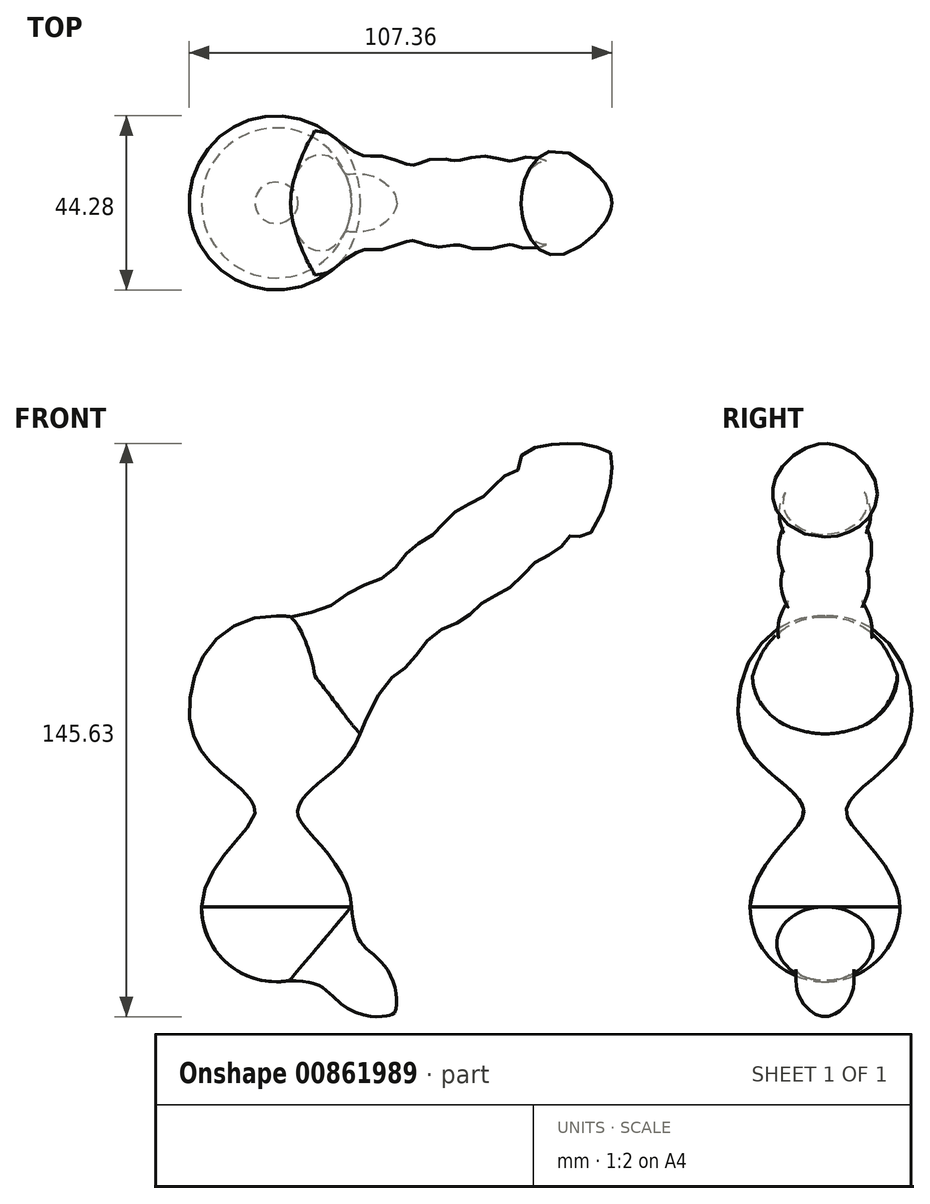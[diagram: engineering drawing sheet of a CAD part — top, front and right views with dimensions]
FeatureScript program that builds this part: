
annotation { "Feature Type Name" : "Feature", "Feature Type Description" : "" }
export const myFeature = defineFeature(function(context is Context, id is Id, definition is map)
    precondition{}
    {
        {
            var Q0;
            Q0=qCreatedBy(makeId("Front.planeOp"),FACE);
            var sketch = newSketch(context, id + "F0", { "sketchPlane" : qUnion([Q0])});
            skArc(sketch, "E0", {"start": v(0, -69.85) * mm, "mid": v(13.47, -64.27) * mm, "end": v(19.05, -50.8) * mm});
            skFitSpline(sketch, "E1", {"points": [v(-0.01, 23.13) * mm, v(21.58, -5.45) * mm, v(9.13, -20.77) * mm, v(5.4, -26.76) * mm, v(8.89, -32.47) * mm, v(19.05, -50.8) * mm], "startDerivative": vector(184.16, 1) * mm, "endDerivative": vector(2.36, -95.96) * mm});
            skLineSegment(sketch, "E2", {"start": v(0, 23.13) * mm, "end": v(0, -69.85) * mm});
            skSolve(sketch);
        }
        {
            var Q0;
            Q0=makeQuery(id+"F0.imprint","IMPRINT",FACE,{"disambiguationData":[TD([[makeQuery(id+"F0.imprint","IMPRINT",EDGE,{"derivedFrom":sQuery(id+"F0.wireOp",EDGE,"E0")}),1.0]])]});
            var Q1;
            Q1=sQuery(id+"F0.wireOp",EDGE,"E2");
            revolve(context, id + "F1", {"surfaceOperationType" : NewSurfaceOperationType.NEW, "entities" : qUnion([Q0]), "axis" : qUnion([Q1]), "revolveType" : RevolveType.FULL});
        }
        {
            var Q0;
            Q0=qCreatedBy(makeId("Front.planeOp"),FACE);
            var sketch = newSketch(context, id + "F2", { "sketchPlane" : qUnion([Q0])});
            skLineSegment(sketch, "E3", {"start": v(0, -50.6) * mm, "end": v(29.97, -77.77) * mm});
            skFitSpline(sketch, "E4", {"points": [v(19.06, -50.8) * mm, v(21.67, -60.14) * mm, v(28.3, -66.98) * mm, v(29.97, -77.77) * mm, v(0, -69.87) * mm], "startDerivative": vector(7.5, -65.65) * mm, "endDerivative": vector(-157.41, 58.8) * mm});
            skLineSegment(sketch, "E5", {"start": v(19.06, -50.8) * mm, "end": v(0, -50.6) * mm});
            skSolve(sketch);
        }
        {
            var Q0;
            Q0=makeQuery(id+"F2.imprint","IMPRINT",FACE,{"disambiguationData":[TD([[makeQuery(id+"F2.imprint","IMPRINT",EDGE,{"derivedFrom":sQuery(id+"F2.wireOp",EDGE,"E3")}),1.0]])]});
            var Q1;
            Q1=sQuery(id+"F2.wireOp",EDGE,"E3");
            revolve(context, id + "F3", {"operationType" : NewBodyOperationType.ADD, "surfaceOperationType" : NewSurfaceOperationType.NEW, "entities" : qUnion([Q0]), "axis" : qUnion([Q1]), "revolveType" : RevolveType.FULL});
        }
        {
            var Q0;
            Q0=qCreatedBy(makeId("Front.planeOp"),FACE);
            var sketch = newSketch(context, id + "F4", { "sketchPlane" : qUnion([Q0])});
            skLineSegment(sketch, "E6", {"start": v(0, 0) * mm, "end": v(84.83, 64.67) * mm});
            skFitSpline(sketch, "E7", {"points": [v(84.83, 64.67) * mm, v(84.83, 56.57) * mm, v(78.49, 43.23) * mm, v(75.2, 43.78) * mm, v(71.9, 40.23) * mm, v(65.99, 36.92) * mm, v(59.6, 30.54) * mm, v(52.75, 26.75) * mm, v(47.3, 22.02) * mm, v(39.98, 18.48) * mm, v(33.76, 10.84) * mm, v(27.55, 5.5) * mm, v(21.16, -6.9) * mm, v(0, 0) * mm], "startDerivative": vector(13.16, -101.21) * mm, "endDerivative": vector(-606.42, -29.56) * mm});
            skSolve(sketch);
        }
        {
            var Q0;
            Q0=makeQuery(id+"F4.imprint","IMPRINT",FACE,{"disambiguationData":[TD([[makeQuery(id+"F4.imprint","IMPRINT",EDGE,{"derivedFrom":sQuery(id+"F4.wireOp",EDGE,"E6")}),-1.0]])]});
            var Q1;
            Q1=sQuery(id+"F4.wireOp",EDGE,"E6");
            revolve(context, id + "F5", {"operationType" : NewBodyOperationType.ADD, "surfaceOperationType" : NewSurfaceOperationType.NEW, "entities" : qUnion([Q0]), "axis" : qUnion([Q1]), "revolveType" : RevolveType.FULL});
        }
    });
